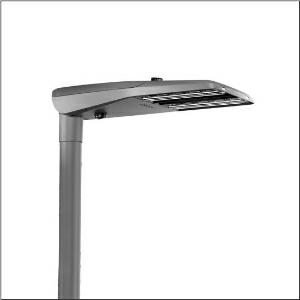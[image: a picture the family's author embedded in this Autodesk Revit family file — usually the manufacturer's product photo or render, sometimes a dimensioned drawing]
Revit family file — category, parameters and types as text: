
# Revit family: streetlight_sl_11_iq_midi___pc-r_5xc3f11y08me_2da3
name_source: partatom
category: Lighting Fixtures
units: mm (PartAtom-declared; Revit-internal decimal feet)

## family parameters
Cut with Voids When Loaded = No
Host = Face
Light Source = No
Part Type = Normal
Room Calculation Point = No
Round Connector Dimension = Use Diameter
Shared = No

## types (1)
- --- (1 x LED, 9610 lm, 123.4 W, 1800K)
    Apparent Load = 123 VA
    CIE Flux Codes = 37 73 96 100 100
    Color Rendering = 70
    Color Temperature = 1800K
    Default Elevation = 1800 mm  [stored 5.90551 ft]
    Description = Streetlight SL 11 iQ midi, mast luminaire, primary light control with 3 zone facetted reflector, of plastic, silver coated, highly specular, primary optical cover: cover, of PMMA, transparent, light distribution: PC-R, light emission: direct distribution, primary light characteristic: asymmetric, right, installation type: post-top, side-entry, lamps: LED, High Power LED, rated values: 9.610lm | 123,4W | 77,9lm/W (begin service life); end service life: 9.610lm | 130,9W; at 50% lumin. flux: 4.805lm | 54,1W | 88,8lm/W, colour temperature: 1800K, colour rendering: CRI > 70, light colour: 718, light setting 1 begin service life: 100% | 9.610lm | 123,4W | 77,9lm/W | 1.800K, light setting 1 end service life: 130,9W, further light settings possible, control: pre-setting: logarithmic dimming characteristic, Street-Remote, Auto-Match, Temp-Guard, Lumen-Switch, Night-Set, Smart-Wire, Light-Fading, Desk-Remote (wireless, voltage-free reading and setting of iQ features in the workshop via application-optimized NFC function/RFID function), optimised constant luminous flux control (CLO 2.0), with cable H07RN-F 3x 1.5mm², mains connection: 230..240V, AC, 50/60Hz, connection cable pre-assembled, cable length: 12,5m, luminaire housing, of diecast aluminium, powder-coated, SITECO metallic grey (DB 702S), please order mast flange separately, inclination adjustable without tools: 0°, 5°, 10°, 15° (post-top) | 0°, -5°, -10°, -15° (side-entry), sealing non-destructively replaceable, multi-level sealing system, length: 780mm, width: 376mm, height: 118mm, mast flange for spigot size: 42mm (side-entry): 5XC10008XM4, 60/48mm (side-entry/post-top): 5XC10108XM2, 76/60mm (side-entry/post-top): 5XC10108XM1, equipment: Power, Smart Interface below and above, protection rating (complete): IP66, insulation class (complete): insulation class II (safety insulation), certification: CE, ENEC, ENEC+, VDE, UKCA, impact resistance: IK10, permissible operating ambient temperature for outdoor applications: -25..+50°C, standard-compliant lighting for roads and squares, Environmental Product Declaration (EPD) tested and certified by an independent institute, packaging unit: 1 piece

Light Distribution: PC-R
    Height = 118 mm
    Lamp = 1 x LED
    Lamp Light Flux = 9610 lm
    Lamp Power = 123.4 W
    Lamp count = 1
    Length = 780 mm
    Luminous efficacy = 78 lm/W
    Manufacturer = Siteco
    ModVariant = No
    Model = 5XC3F11Y08ME
    Number of Poles = 1
    OnlyDefault = Yes
    Power Factor = 1
    Product Name = Streetlight SL 11 iQ midi | PC-R
    Product group = mast luminaire | pylon top
    ProductGroupID = 6100
    Protection Class = Protection class II
    Protection Degree = IP 66
    RLX_Detail_Level = 1
    RLX_Emergency_Light_Flux = 0 lm
    RLX_Emergency_Type = 0
    RLX_Emergency_Type_DB = No
    RlxData = <blob elided: 73657 chars, md5=85b45137>
    Socket = socket
    Standby Power = 0 W
    System Light Flux = 9610 lm
    System Power = 123 W
    Type Comments = factory setting: luminous flux: 100 % | dim-lin: 254 | 553 mA
    Type Image = l_1004429.jpg
    URL = http://relux.com
    VarID = @adj_038943
    Voltage = 0 V
    Weight = 0.00 kg
    Width = 376 mm

note: [stored X ft] marks values corroborated as IEEE doubles in the binary element streams (Revit-internal decimal feet)

## geometry (parser evidence)
native form markers: Blend x4, Sweep x11
no freeform markers — native parametric forms only
